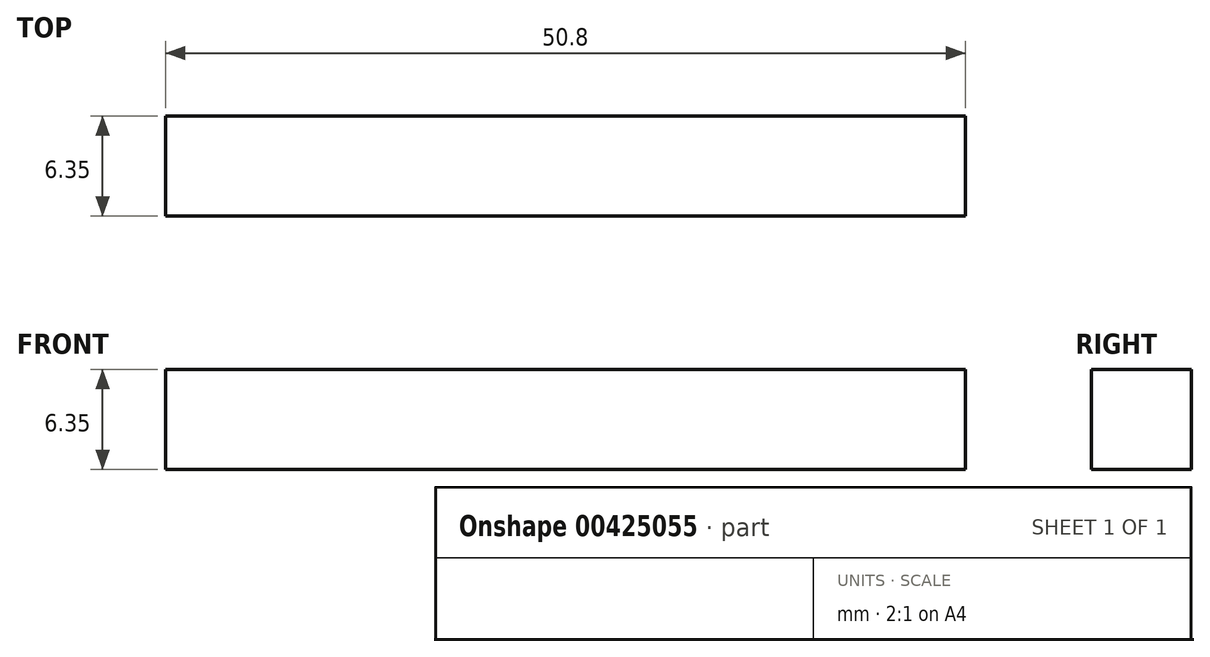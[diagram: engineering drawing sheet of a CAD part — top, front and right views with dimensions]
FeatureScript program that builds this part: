
annotation { "Feature Type Name" : "Feature", "Feature Type Description" : "" }
export const myFeature = defineFeature(function(context is Context, id is Id, definition is map)
    precondition{}
    {
        {
            var Q0;
            Q0=qCreatedBy(makeId("Front.planeOp"),FACE);
            var sketch = newSketch(context, id + "F0", { "sketchPlane" : qUnion([Q0])});
            skLineSegment(sketch, "E0.bottom", {"start": v(-29.39, 10.87) * mm, "end": v(21.41, 10.87) * mm});
            skLineSegment(sketch, "E0.top", {"start": v(-29.39, 4.52) * mm, "end": v(21.41, 4.52) * mm});
            skLineSegment(sketch, "E0.left", {"start": v(-29.39, 10.87) * mm, "end": v(-29.39, 4.52) * mm});
            skLineSegment(sketch, "E0.right", {"start": v(21.41, 10.87) * mm, "end": v(21.41, 4.52) * mm});
            skSolve(sketch);
        }
        {
            var Q0;
            Q0 = qSketchRegion(id + "F0", true);
            extrude(context, id + "F1", {"entities" : qUnion([Q0]), "depth" : 6.35 * mm});
        }
    });
